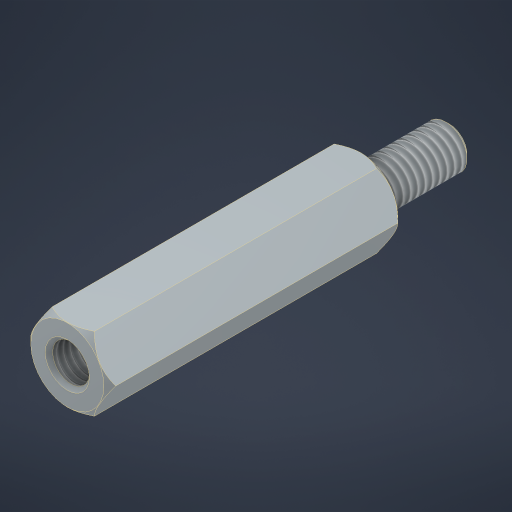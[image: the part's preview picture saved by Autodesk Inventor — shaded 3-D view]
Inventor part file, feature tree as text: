
AUTODESK INVENTOR PART (.ipt)
format: ipt  version: 2023 (Build 270158000, 158)  size: 235,520 bytes
history: mixed  units: in
note: dims shown in document units (in); Inventor stores cm internally (conversion verified against a paired STEP export)
features: thread x2, other x1, imported_body x1
ambient origin geometry x8: Origin, YZ Plane, XZ Plane, XY Plane, X Axis, Y Axis, Z Axis, Center Point
bodies: Solid1 (imported_parasolid)
feature tree (4):
  thread  "Thread1"  [1 undecoded]
  thread  "Thread2"  [1 undecoded]
  other  "InnerChamfer"
  imported_body  NMx_Import_Brep_tag  [imported B-rep: ~6 faces, bbox_mm=None]
note: 2 required parameter values undecoded (feature->parameter linkage not recoverable at this tier; creation-order binding heuristic only, values carry confidence <= 0.55)
